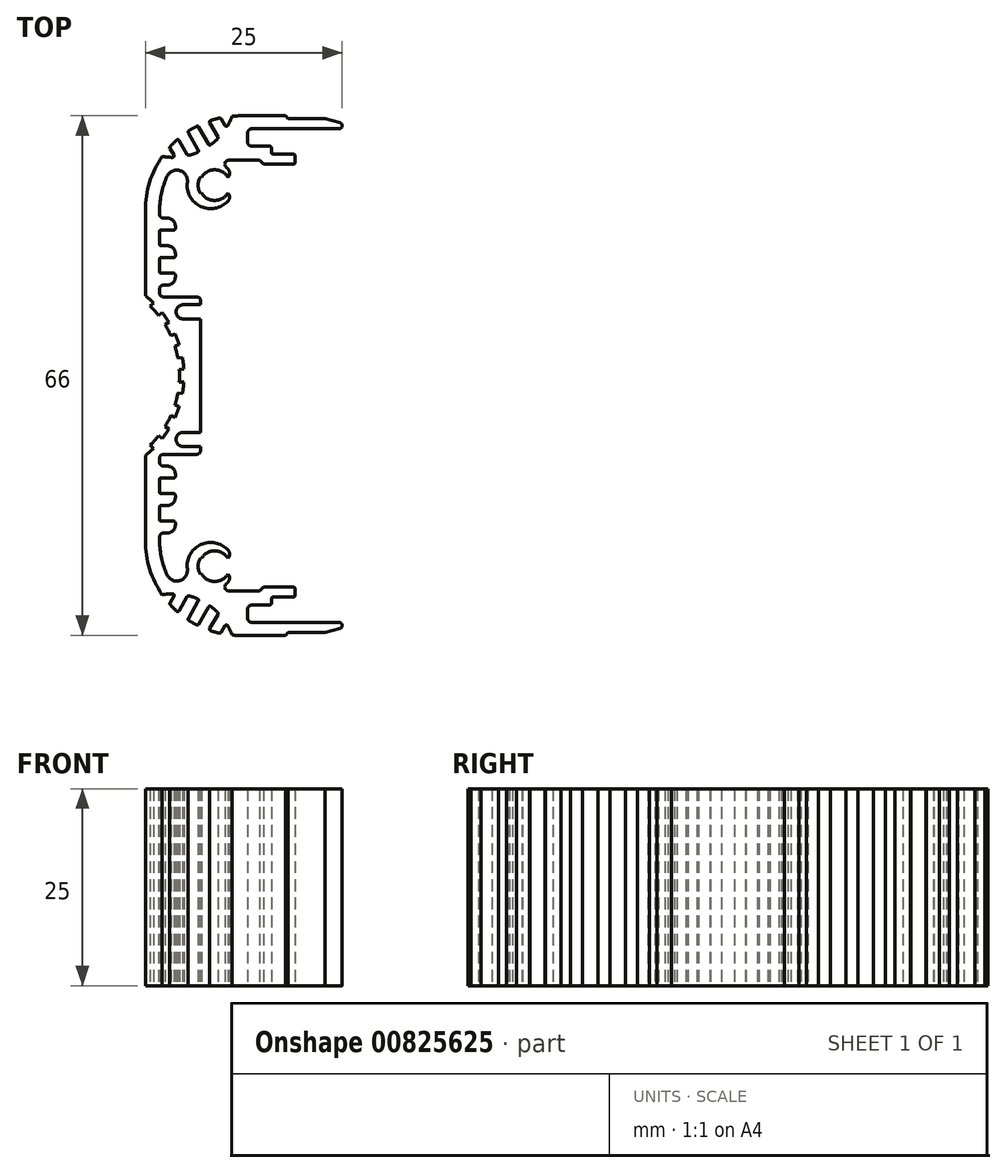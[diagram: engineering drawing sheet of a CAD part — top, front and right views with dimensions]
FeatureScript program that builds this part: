
annotation { "Feature Type Name" : "Feature", "Feature Type Description" : "" }
export const myFeature = defineFeature(function(context is Context, id is Id, definition is map)
    precondition{}
    {
        {
            var Q0;
            Q0=qCreatedBy(makeId("Top.planeOp"),FACE);
            var sketch = newSketch(context, id + "F0", { "sketchPlane" : qUnion([Q0])});
            skArc(sketch, "E0", {"start": v(4.8, 42) * mm, "mid": v(3.9, 41.1) * mm, "end": v(4.8, 40.2) * mm});
            skLineSegment(sketch, "E1", {"start": v(4.8, 42) * mm, "end": v(7, 42) * mm});
            skLineSegment(sketch, "E2", {"start": v(7, 42) * mm, "end": v(7, 42.5) * mm});
            skArc(sketch, "E3", {"start": v(7, 42.5) * mm, "mid": v(6.85, 42.85) * mm, "end": v(6.5, 43) * mm});
            skLineSegment(sketch, "E4", {"start": v(6.5, 43) * mm, "end": v(2.3, 43) * mm});
            skArc(sketch, "E5", {"start": v(1.8, 43.5) * mm, "mid": v(1.95, 43.15) * mm, "end": v(2.3, 43) * mm});
            skLineSegment(sketch, "E6", {"start": v(1.8, 43.5) * mm, "end": v(1.8, 44) * mm});
            skArc(sketch, "E7", {"start": v(2.3, 44.5) * mm, "mid": v(1.95, 44.35) * mm, "end": v(1.8, 44) * mm});
            skLineSegment(sketch, "E8", {"start": v(2.3, 44.5) * mm, "end": v(2.8, 44.5) * mm});
            skArc(sketch, "E9", {"start": v(2.8, 44.5) * mm, "mid": v(3.5, 44.8) * mm, "end": v(3.8, 45.5) * mm});
            skLineSegment(sketch, "E10", {"start": v(3.8, 45.5) * mm, "end": v(3.8, 45.8) * mm});
            skArc(sketch, "E11", {"start": v(3.8, 45.8) * mm, "mid": v(3.74, 45.94) * mm, "end": v(3.6, 46) * mm});
            skLineSegment(sketch, "E12", {"start": v(3.6, 46) * mm, "end": v(2, 46) * mm});
            skArc(sketch, "E13", {"start": v(1.8, 46.2) * mm, "mid": v(1.86, 46.06) * mm, "end": v(2, 46) * mm});
            skLineSegment(sketch, "E14", {"start": v(1.8, 46.2) * mm, "end": v(1.8, 47.8) * mm});
            skArc(sketch, "E15", {"start": v(2, 48) * mm, "mid": v(1.86, 47.94) * mm, "end": v(1.8, 47.8) * mm});
            skLineSegment(sketch, "E16", {"start": v(2, 48) * mm, "end": v(3.6, 48) * mm});
            skArc(sketch, "E17", {"start": v(3.6, 48) * mm, "mid": v(3.74, 48.06) * mm, "end": v(3.8, 48.2) * mm});
            skLineSegment(sketch, "E18", {"start": v(3.8, 48.2) * mm, "end": v(3.8, 48.5) * mm});
            skArc(sketch, "E19", {"start": v(3.8, 48.5) * mm, "mid": v(3.5, 49.2) * mm, "end": v(2.8, 49.5) * mm});
            skLineSegment(sketch, "E20", {"start": v(2.8, 49.5) * mm, "end": v(2, 49.5) * mm});
            skArc(sketch, "E21", {"start": v(1.8, 49.7) * mm, "mid": v(1.86, 49.56) * mm, "end": v(2, 49.5) * mm});
            skLineSegment(sketch, "E22", {"start": v(1.8, 49.7) * mm, "end": v(1.8, 51.3) * mm});
            skArc(sketch, "E23", {"start": v(2, 51.5) * mm, "mid": v(1.86, 51.44) * mm, "end": v(1.8, 51.3) * mm});
            skLineSegment(sketch, "E24", {"start": v(2, 51.5) * mm, "end": v(3.6, 51.5) * mm});
            skArc(sketch, "E25", {"start": v(3.6, 51.5) * mm, "mid": v(3.74, 51.56) * mm, "end": v(3.8, 51.7) * mm});
            skLineSegment(sketch, "E26", {"start": v(3.8, 51.7) * mm, "end": v(3.8, 52) * mm});
            skArc(sketch, "E27", {"start": v(3.8, 52) * mm, "mid": v(3.5, 52.7) * mm, "end": v(2.8, 53) * mm});
            skLineSegment(sketch, "E28", {"start": v(2.8, 53) * mm, "end": v(2.3, 53) * mm});
            skArc(sketch, "E29", {"start": v(1.8, 53.5) * mm, "mid": v(1.95, 53.15) * mm, "end": v(2.3, 53) * mm});
            skLineSegment(sketch, "E30", {"start": v(1.8, 53.5) * mm, "end": v(1.8, 54) * mm});
            skArc(sketch, "E31", {"start": v(2.76, 58.33) * mm, "mid": v(2.04, 56.22) * mm, "end": v(1.8, 54) * mm});
            skArc(sketch, "E32", {"start": v(5.32, 57.58) * mm, "mid": v(4.36, 59.05) * mm, "end": v(2.76, 58.33) * mm});
            skArc(sketch, "E33", {"start": v(5.32, 57.58) * mm, "mid": v(7.03, 54.48) * mm, "end": v(10.5, 55.16) * mm});
            skArc(sketch, "E34", {"start": v(10.5, 55.16) * mm, "mid": v(10.7, 55.69) * mm, "end": v(10.48, 56.2) * mm});
            skArc(sketch, "E35", {"start": v(7.11, 56.23) * mm, "mid": v(8.79, 55.25) * mm, "end": v(10.48, 56.2) * mm});
            skLineSegment(sketch, "E36", {"start": v(7.11, 56.23) * mm, "end": v(6.98, 56.15) * mm});
            skArc(sketch, "E37", {"start": v(6.98, 58.25) * mm, "mid": v(6.7, 57.2) * mm, "end": v(6.98, 56.15) * mm});
            skLineSegment(sketch, "E38", {"start": v(6.98, 58.25) * mm, "end": v(7.11, 58.17) * mm});
            skArc(sketch, "E39", {"start": v(10.48, 58.2) * mm, "mid": v(8.79, 59.15) * mm, "end": v(7.11, 58.17) * mm});
            skArc(sketch, "E40", {"start": v(10.48, 58.2) * mm, "mid": v(10.7, 58.71) * mm, "end": v(10.5, 59.24) * mm});
            skArc(sketch, "E41", {"start": v(10.5, 59.24) * mm, "mid": v(10.38, 59.36) * mm, "end": v(10.26, 59.47) * mm});
            skArc(sketch, "E42", {"start": v(10.59, 60.35) * mm, "mid": v(10.12, 60.02) * mm, "end": v(10.26, 59.47) * mm});
            skLineSegment(sketch, "E43", {"start": v(10.59, 60.35) * mm, "end": v(14.5, 60.35) * mm});
            skLineSegment(sketch, "E44", {"start": v(14.5, 60.35) * mm, "end": v(15, 59.85) * mm});
            skLineSegment(sketch, "E45", {"start": v(15, 59.85) * mm, "end": v(18.8, 59.85) * mm});
            skArc(sketch, "E46", {"start": v(18.8, 59.85) * mm, "mid": v(18.94, 59.9) * mm, "end": v(19, 60.05) * mm});
            skLineSegment(sketch, "E47", {"start": v(19, 60.05) * mm, "end": v(19, 60.95) * mm});
            skArc(sketch, "E48", {"start": v(19, 60.95) * mm, "mid": v(18.94, 61.1) * mm, "end": v(18.8, 61.15) * mm});
            skLineSegment(sketch, "E49", {"start": v(18.8, 61.15) * mm, "end": v(16.2, 61.15) * mm});
            skArc(sketch, "E50", {"start": v(16, 61.35) * mm, "mid": v(16.06, 61.2) * mm, "end": v(16.2, 61.15) * mm});
            skLineSegment(sketch, "E51", {"start": v(16, 61.35) * mm, "end": v(16, 61.95) * mm});
            skArc(sketch, "E52", {"start": v(16, 61.95) * mm, "mid": v(15.94, 62.1) * mm, "end": v(15.8, 62.15) * mm});
            skLineSegment(sketch, "E53", {"start": v(15.8, 62.15) * mm, "end": v(13.5, 62.15) * mm});
            skArc(sketch, "E54", {"start": v(13, 62.65) * mm, "mid": v(13.15, 62.3) * mm, "end": v(13.5, 62.15) * mm});
            skLineSegment(sketch, "E55", {"start": v(13, 62.65) * mm, "end": v(13, 63.85) * mm});
            skArc(sketch, "E56", {"start": v(13.5, 64.35) * mm, "mid": v(13.15, 64.2) * mm, "end": v(13, 63.85) * mm});
            skLineSegment(sketch, "E57", {"start": v(13.5, 64.35) * mm, "end": v(24.6, 64.35) * mm});
            skArc(sketch, "E58", {"start": v(24.6, 64.35) * mm, "mid": v(25, 64.7) * mm, "end": v(24.7, 65.14) * mm});
            skLineSegment(sketch, "E59", {"start": v(24.7, 65.14) * mm, "end": v(22.79, 65.65) * mm});
            skLineSegment(sketch, "E60", {"start": v(22.79, 65.65) * mm, "end": v(18.15, 65.65) * mm});
            skLineSegment(sketch, "E61", {"start": v(18.15, 65.65) * mm, "end": v(17.8, 66) * mm});
            skLineSegment(sketch, "E62", {"start": v(17.8, 66) * mm, "end": v(12, 66) * mm});
            skArc(sketch, "E63", {"start": v(12, 66) * mm, "mid": v(11.5, 65.99) * mm, "end": v(11, 65.96) * mm});
            skArc(sketch, "E64", {"start": v(10.46, 64.77) * mm, "mid": v(10.76, 65.36) * mm, "end": v(11, 65.96) * mm});
            skArc(sketch, "E65", {"start": v(10.11, 64.77) * mm, "mid": v(10.29, 64.67) * mm, "end": v(10.46, 64.77) * mm});
            skLineSegment(sketch, "E66", {"start": v(10.11, 64.77) * mm, "end": v(9.62, 65.62) * mm});
            skArc(sketch, "E67", {"start": v(9.62, 65.62) * mm, "mid": v(9.53, 65.7) * mm, "end": v(9.4, 65.72) * mm});
            skArc(sketch, "E68", {"start": v(9.4, 65.72) * mm, "mid": v(8.84, 65.58) * mm, "end": v(8.29, 65.41) * mm});
            skArc(sketch, "E69", {"start": v(8.29, 65.41) * mm, "mid": v(8.16, 65.3) * mm, "end": v(8.18, 65.12) * mm});
            skLineSegment(sketch, "E70", {"start": v(8.18, 65.12) * mm, "end": v(9.21, 63.33) * mm});
            skArc(sketch, "E71", {"start": v(9.18, 63.09) * mm, "mid": v(9.24, 63.2) * mm, "end": v(9.21, 63.33) * mm});
            skArc(sketch, "E72", {"start": v(8.32, 62.33) * mm, "mid": v(8.76, 62.7) * mm, "end": v(9.18, 63.09) * mm});
            skArc(sketch, "E73", {"start": v(8.02, 62.4) * mm, "mid": v(8.16, 62.3) * mm, "end": v(8.32, 62.33) * mm});
            skLineSegment(sketch, "E74", {"start": v(8.02, 62.4) * mm, "end": v(6.76, 64.58) * mm});
            skArc(sketch, "E75", {"start": v(6.76, 64.58) * mm, "mid": v(6.64, 64.68) * mm, "end": v(6.5, 64.66) * mm});
            skArc(sketch, "E76", {"start": v(6.5, 64.66) * mm, "mid": v(6, 64.4) * mm, "end": v(5.52, 64.1) * mm});
            skArc(sketch, "E77", {"start": v(5.52, 64.1) * mm, "mid": v(5.43, 63.98) * mm, "end": v(5.46, 63.83) * mm});
            skLineSegment(sketch, "E78", {"start": v(5.46, 63.83) * mm, "end": v(6.72, 61.64) * mm});
            skArc(sketch, "E79", {"start": v(6.63, 61.36) * mm, "mid": v(6.74, 61.48) * mm, "end": v(6.72, 61.64) * mm});
            skArc(sketch, "E80", {"start": v(5.54, 60.98) * mm, "mid": v(6.09, 61.15) * mm, "end": v(6.63, 61.36) * mm});
            skArc(sketch, "E81", {"start": v(5.31, 61.08) * mm, "mid": v(5.41, 61) * mm, "end": v(5.54, 60.98) * mm});
            skLineSegment(sketch, "E82", {"start": v(5.31, 61.08) * mm, "end": v(4.28, 62.87) * mm});
            skArc(sketch, "E83", {"start": v(4.28, 62.87) * mm, "mid": v(4.14, 62.97) * mm, "end": v(3.97, 62.92) * mm});
            skArc(sketch, "E84", {"start": v(3.97, 62.92) * mm, "mid": v(3.55, 62.52) * mm, "end": v(3.15, 62.1) * mm});
            skArc(sketch, "E85", {"start": v(3.15, 62.1) * mm, "mid": v(3.1, 62) * mm, "end": v(3.12, 61.87) * mm});
            skLineSegment(sketch, "E86", {"start": v(3.12, 61.87) * mm, "end": v(3.62, 61.02) * mm});
            skArc(sketch, "E87", {"start": v(3.44, 60.72) * mm, "mid": v(3.61, 60.82) * mm, "end": v(3.62, 61.02) * mm});
            skArc(sketch, "E88", {"start": v(2.14, 60.84) * mm, "mid": v(2.79, 60.75) * mm, "end": v(3.44, 60.72) * mm});
            skArc(sketch, "E89", {"start": v(2.14, 60.84) * mm, "mid": v(0.55, 57.58) * mm, "end": v(0, 54) * mm});
            skLineSegment(sketch, "E90", {"start": v(0, 54) * mm, "end": v(0, 43.13) * mm});
            skArc(sketch, "E91", {"start": v(1.01, 42.24) * mm, "mid": v(0.52, 42.7) * mm, "end": v(0, 43.13) * mm});
            skLineSegment(sketch, "E92", {"start": v(1.01, 42.24) * mm, "end": v(0.6, 41.83) * mm});
            skArc(sketch, "E93", {"start": v(1.68, 40.64) * mm, "mid": v(1.16, 41.25) * mm, "end": v(0.6, 41.83) * mm});
            skLineSegment(sketch, "E94", {"start": v(1.68, 40.64) * mm, "end": v(2.13, 41) * mm});
            skArc(sketch, "E95", {"start": v(2.98, 39.79) * mm, "mid": v(2.58, 40.4) * mm, "end": v(2.13, 41) * mm});
            skLineSegment(sketch, "E96", {"start": v(2.98, 39.79) * mm, "end": v(2.49, 39.48) * mm});
            skArc(sketch, "E97", {"start": v(3.24, 38.07) * mm, "mid": v(2.89, 38.79) * mm, "end": v(2.49, 39.48) * mm});
            skLineSegment(sketch, "E98", {"start": v(3.24, 38.07) * mm, "end": v(3.77, 38.3) * mm});
            skArc(sketch, "E99", {"start": v(4.3, 36.93) * mm, "mid": v(4.05, 37.63) * mm, "end": v(3.77, 38.3) * mm});
            skLineSegment(sketch, "E100", {"start": v(4.3, 36.93) * mm, "end": v(3.75, 36.75) * mm});
            skArc(sketch, "E101", {"start": v(4.13, 35.2) * mm, "mid": v(3.96, 35.98) * mm, "end": v(3.75, 36.75) * mm});
            skLineSegment(sketch, "E102", {"start": v(4.13, 35.2) * mm, "end": v(4.7, 35.3) * mm});
            skArc(sketch, "E103", {"start": v(4.88, 33.84) * mm, "mid": v(4.81, 34.57) * mm, "end": v(4.7, 35.3) * mm});
            skLineSegment(sketch, "E104", {"start": v(4.88, 33.84) * mm, "end": v(4.3, 33.8) * mm});
            skArc(sketch, "E105", {"start": v(4.3, 32.2) * mm, "mid": v(4.33, 33) * mm, "end": v(4.3, 33.8) * mm});
            skLineSegment(sketch, "E106", {"start": v(4.3, 32.2) * mm, "end": v(4.88, 32.16) * mm});
            skArc(sketch, "E107", {"start": v(4.7, 30.7) * mm, "mid": v(4.81, 31.43) * mm, "end": v(4.88, 32.16) * mm});
            skLineSegment(sketch, "E108", {"start": v(4.7, 30.7) * mm, "end": v(4.13, 30.8) * mm});
            skArc(sketch, "E109", {"start": v(3.75, 29.25) * mm, "mid": v(3.96, 30.02) * mm, "end": v(4.13, 30.8) * mm});
            skLineSegment(sketch, "E110", {"start": v(3.75, 29.25) * mm, "end": v(4.3, 29.07) * mm});
            skArc(sketch, "E111", {"start": v(3.77, 27.7) * mm, "mid": v(4.05, 28.37) * mm, "end": v(4.3, 29.07) * mm});
            skLineSegment(sketch, "E112", {"start": v(3.77, 27.7) * mm, "end": v(3.24, 27.93) * mm});
            skArc(sketch, "E113", {"start": v(2.49, 26.52) * mm, "mid": v(2.89, 27.21) * mm, "end": v(3.24, 27.93) * mm});
            skLineSegment(sketch, "E114", {"start": v(2.49, 26.52) * mm, "end": v(2.98, 26.21) * mm});
            skArc(sketch, "E115", {"start": v(2.13, 25) * mm, "mid": v(2.58, 25.6) * mm, "end": v(2.98, 26.21) * mm});
            skLineSegment(sketch, "E116", {"start": v(2.13, 25) * mm, "end": v(1.68, 25.36) * mm});
            skArc(sketch, "E117", {"start": v(0.6, 24.17) * mm, "mid": v(1.16, 24.75) * mm, "end": v(1.68, 25.36) * mm});
            skLineSegment(sketch, "E118", {"start": v(0.6, 24.17) * mm, "end": v(1.01, 23.76) * mm});
            skArc(sketch, "E119", {"start": v(0, 22.87) * mm, "mid": v(0.52, 23.3) * mm, "end": v(1.01, 23.76) * mm});
            skLineSegment(sketch, "E120", {"start": v(0, 22.87) * mm, "end": v(0, 12) * mm});
            skArc(sketch, "E121", {"start": v(0, 12) * mm, "mid": v(0.55, 8.42) * mm, "end": v(2.14, 5.16) * mm});
            skArc(sketch, "E122", {"start": v(3.44, 5.28) * mm, "mid": v(2.79, 5.25) * mm, "end": v(2.14, 5.16) * mm});
            skArc(sketch, "E123", {"start": v(3.62, 4.98) * mm, "mid": v(3.61, 5.18) * mm, "end": v(3.44, 5.28) * mm});
            skLineSegment(sketch, "E124", {"start": v(3.62, 4.98) * mm, "end": v(3.12, 4.13) * mm});
            skArc(sketch, "E125", {"start": v(3.12, 4.13) * mm, "mid": v(3.1, 4) * mm, "end": v(3.15, 3.9) * mm});
            skArc(sketch, "E126", {"start": v(3.15, 3.9) * mm, "mid": v(3.55, 3.48) * mm, "end": v(3.97, 3.08) * mm});
            skArc(sketch, "E127", {"start": v(3.97, 3.08) * mm, "mid": v(4.14, 3.03) * mm, "end": v(4.28, 3.13) * mm});
            skLineSegment(sketch, "E128", {"start": v(4.28, 3.13) * mm, "end": v(5.31, 4.92) * mm});
            skArc(sketch, "E129", {"start": v(5.54, 5.02) * mm, "mid": v(5.41, 5) * mm, "end": v(5.31, 4.92) * mm});
            skArc(sketch, "E130", {"start": v(6.63, 4.64) * mm, "mid": v(6.09, 4.85) * mm, "end": v(5.54, 5.02) * mm});
            skArc(sketch, "E131", {"start": v(6.72, 4.36) * mm, "mid": v(6.74, 4.52) * mm, "end": v(6.63, 4.64) * mm});
            skLineSegment(sketch, "E132", {"start": v(6.72, 4.36) * mm, "end": v(5.46, 2.17) * mm});
            skArc(sketch, "E133", {"start": v(5.46, 2.17) * mm, "mid": v(5.43, 2.02) * mm, "end": v(5.52, 1.9) * mm});
            skArc(sketch, "E134", {"start": v(5.52, 1.9) * mm, "mid": v(6, 1.6) * mm, "end": v(6.5, 1.34) * mm});
            skArc(sketch, "E135", {"start": v(6.5, 1.34) * mm, "mid": v(6.64, 1.32) * mm, "end": v(6.76, 1.42) * mm});
            skLineSegment(sketch, "E136", {"start": v(6.76, 1.42) * mm, "end": v(8.02, 3.6) * mm});
            skArc(sketch, "E137", {"start": v(8.32, 3.67) * mm, "mid": v(8.16, 3.7) * mm, "end": v(8.02, 3.6) * mm});
            skArc(sketch, "E138", {"start": v(9.18, 2.91) * mm, "mid": v(8.76, 3.3) * mm, "end": v(8.32, 3.67) * mm});
            skArc(sketch, "E139", {"start": v(9.21, 2.67) * mm, "mid": v(9.24, 2.8) * mm, "end": v(9.18, 2.91) * mm});
            skLineSegment(sketch, "E140", {"start": v(9.21, 2.67) * mm, "end": v(8.18, 0.88) * mm});
            skArc(sketch, "E141", {"start": v(8.18, 0.88) * mm, "mid": v(8.16, 0.7) * mm, "end": v(8.29, 0.59) * mm});
            skArc(sketch, "E142", {"start": v(8.29, 0.59) * mm, "mid": v(8.84, 0.42) * mm, "end": v(9.4, 0.28) * mm});
            skArc(sketch, "E143", {"start": v(9.4, 0.28) * mm, "mid": v(9.53, 0.3) * mm, "end": v(9.62, 0.38) * mm});
            skLineSegment(sketch, "E144", {"start": v(9.62, 0.38) * mm, "end": v(10.11, 1.23) * mm});
            skArc(sketch, "E145", {"start": v(10.46, 1.23) * mm, "mid": v(10.29, 1.33) * mm, "end": v(10.11, 1.23) * mm});
            skArc(sketch, "E146", {"start": v(11, 0.04) * mm, "mid": v(10.76, 0.64) * mm, "end": v(10.46, 1.23) * mm});
            skArc(sketch, "E147", {"start": v(11, 0.04) * mm, "mid": v(11.5, 0.01) * mm, "end": v(12, 0) * mm});
            skLineSegment(sketch, "E148", {"start": v(12, 0) * mm, "end": v(17.8, 0) * mm});
            skLineSegment(sketch, "E149", {"start": v(17.8, 0) * mm, "end": v(18.15, 0.35) * mm});
            skLineSegment(sketch, "E150", {"start": v(18.15, 0.35) * mm, "end": v(22.79, 0.35) * mm});
            skLineSegment(sketch, "E151", {"start": v(22.79, 0.35) * mm, "end": v(24.7, 0.86) * mm});
            skArc(sketch, "E152", {"start": v(24.7, 0.86) * mm, "mid": v(25, 1.3) * mm, "end": v(24.6, 1.65) * mm});
            skLineSegment(sketch, "E153", {"start": v(24.6, 1.65) * mm, "end": v(13.5, 1.65) * mm});
            skArc(sketch, "E154", {"start": v(13, 2.15) * mm, "mid": v(13.15, 1.8) * mm, "end": v(13.5, 1.65) * mm});
            skLineSegment(sketch, "E155", {"start": v(13, 2.15) * mm, "end": v(13, 3.35) * mm});
            skArc(sketch, "E156", {"start": v(13.5, 3.85) * mm, "mid": v(13.15, 3.7) * mm, "end": v(13, 3.35) * mm});
            skLineSegment(sketch, "E157", {"start": v(13.5, 3.85) * mm, "end": v(15.8, 3.85) * mm});
            skArc(sketch, "E158", {"start": v(15.8, 3.85) * mm, "mid": v(15.94, 3.9) * mm, "end": v(16, 4.05) * mm});
            skLineSegment(sketch, "E159", {"start": v(16, 4.05) * mm, "end": v(16, 4.65) * mm});
            skArc(sketch, "E160", {"start": v(16.2, 4.85) * mm, "mid": v(16.06, 4.8) * mm, "end": v(16, 4.65) * mm});
            skLineSegment(sketch, "E161", {"start": v(16.2, 4.85) * mm, "end": v(18.8, 4.85) * mm});
            skArc(sketch, "E162", {"start": v(18.8, 4.85) * mm, "mid": v(18.94, 4.9) * mm, "end": v(19, 5.05) * mm});
            skLineSegment(sketch, "E163", {"start": v(19, 5.05) * mm, "end": v(19, 5.95) * mm});
            skArc(sketch, "E164", {"start": v(19, 5.95) * mm, "mid": v(18.94, 6.1) * mm, "end": v(18.8, 6.15) * mm});
            skLineSegment(sketch, "E165", {"start": v(18.8, 6.15) * mm, "end": v(15, 6.15) * mm});
            skLineSegment(sketch, "E166", {"start": v(15, 6.15) * mm, "end": v(14.5, 5.65) * mm});
            skLineSegment(sketch, "E167", {"start": v(14.5, 5.65) * mm, "end": v(10.59, 5.65) * mm});
            skArc(sketch, "E168", {"start": v(10.26, 6.53) * mm, "mid": v(10.12, 5.98) * mm, "end": v(10.59, 5.65) * mm});
            skArc(sketch, "E169", {"start": v(10.26, 6.53) * mm, "mid": v(10.38, 6.64) * mm, "end": v(10.5, 6.76) * mm});
            skArc(sketch, "E170", {"start": v(10.5, 6.76) * mm, "mid": v(10.7, 7.29) * mm, "end": v(10.48, 7.8) * mm});
            skArc(sketch, "E171", {"start": v(7.11, 7.83) * mm, "mid": v(8.79, 6.85) * mm, "end": v(10.48, 7.8) * mm});
            skLineSegment(sketch, "E172", {"start": v(7.11, 7.83) * mm, "end": v(6.98, 7.75) * mm});
            skArc(sketch, "E173", {"start": v(6.98, 9.85) * mm, "mid": v(6.7, 8.8) * mm, "end": v(6.98, 7.75) * mm});
            skLineSegment(sketch, "E174", {"start": v(6.98, 9.85) * mm, "end": v(7.11, 9.78) * mm});
            skArc(sketch, "E175", {"start": v(10.48, 9.8) * mm, "mid": v(8.79, 10.75) * mm, "end": v(7.11, 9.77) * mm});
            skArc(sketch, "E176", {"start": v(10.48, 9.8) * mm, "mid": v(10.7, 10.31) * mm, "end": v(10.5, 10.84) * mm});
            skArc(sketch, "E177", {"start": v(10.5, 10.84) * mm, "mid": v(7.03, 11.52) * mm, "end": v(5.32, 8.42) * mm});
            skArc(sketch, "E178", {"start": v(2.76, 7.67) * mm, "mid": v(4.36, 6.95) * mm, "end": v(5.32, 8.42) * mm});
            skArc(sketch, "E179", {"start": v(1.8, 12) * mm, "mid": v(2.04, 9.78) * mm, "end": v(2.76, 7.67) * mm});
            skLineSegment(sketch, "E180", {"start": v(1.8, 12) * mm, "end": v(1.8, 12.5) * mm});
            skArc(sketch, "E181", {"start": v(2.3, 13) * mm, "mid": v(1.95, 12.85) * mm, "end": v(1.8, 12.5) * mm});
            skLineSegment(sketch, "E182", {"start": v(2.3, 13) * mm, "end": v(2.8, 13) * mm});
            skArc(sketch, "E183", {"start": v(2.8, 13) * mm, "mid": v(3.5, 13.3) * mm, "end": v(3.8, 14) * mm});
            skLineSegment(sketch, "E184", {"start": v(3.8, 14) * mm, "end": v(3.8, 14.3) * mm});
            skArc(sketch, "E185", {"start": v(3.8, 14.3) * mm, "mid": v(3.74, 14.44) * mm, "end": v(3.6, 14.5) * mm});
            skLineSegment(sketch, "E186", {"start": v(3.6, 14.5) * mm, "end": v(2, 14.5) * mm});
            skArc(sketch, "E187", {"start": v(1.8, 14.7) * mm, "mid": v(1.86, 14.56) * mm, "end": v(2, 14.5) * mm});
            skLineSegment(sketch, "E188", {"start": v(1.8, 14.7) * mm, "end": v(1.8, 16.3) * mm});
            skArc(sketch, "E189", {"start": v(2, 16.5) * mm, "mid": v(1.86, 16.44) * mm, "end": v(1.8, 16.3) * mm});
            skLineSegment(sketch, "E190", {"start": v(2, 16.5) * mm, "end": v(2.8, 16.5) * mm});
            skArc(sketch, "E191", {"start": v(2.8, 16.5) * mm, "mid": v(3.5, 16.8) * mm, "end": v(3.8, 17.5) * mm});
            skLineSegment(sketch, "E192", {"start": v(3.8, 17.5) * mm, "end": v(3.8, 17.8) * mm});
            skArc(sketch, "E193", {"start": v(3.8, 17.8) * mm, "mid": v(3.74, 17.94) * mm, "end": v(3.6, 18) * mm});
            skLineSegment(sketch, "E194", {"start": v(3.6, 18) * mm, "end": v(2, 18) * mm});
            skArc(sketch, "E195", {"start": v(1.8, 18.2) * mm, "mid": v(1.86, 18.06) * mm, "end": v(2, 18) * mm});
            skLineSegment(sketch, "E196", {"start": v(1.8, 18.2) * mm, "end": v(1.8, 19.8) * mm});
            skArc(sketch, "E197", {"start": v(2, 20) * mm, "mid": v(1.86, 19.94) * mm, "end": v(1.8, 19.8) * mm});
            skLineSegment(sketch, "E198", {"start": v(2, 20) * mm, "end": v(3.6, 20) * mm});
            skArc(sketch, "E199", {"start": v(3.6, 20) * mm, "mid": v(3.74, 20.06) * mm, "end": v(3.8, 20.2) * mm});
            skLineSegment(sketch, "E200", {"start": v(3.8, 20.2) * mm, "end": v(3.8, 20.5) * mm});
            skArc(sketch, "E201", {"start": v(3.8, 20.5) * mm, "mid": v(3.5, 21.2) * mm, "end": v(2.8, 21.5) * mm});
            skLineSegment(sketch, "E202", {"start": v(2.8, 21.5) * mm, "end": v(2.3, 21.5) * mm});
            skArc(sketch, "E203", {"start": v(1.8, 22) * mm, "mid": v(1.95, 21.65) * mm, "end": v(2.3, 21.5) * mm});
            skLineSegment(sketch, "E204", {"start": v(1.8, 22) * mm, "end": v(1.8, 22.5) * mm});
            skArc(sketch, "E205", {"start": v(2.3, 23) * mm, "mid": v(1.95, 22.85) * mm, "end": v(1.8, 22.5) * mm});
            skLineSegment(sketch, "E206", {"start": v(2.3, 23) * mm, "end": v(6.5, 23) * mm});
            skArc(sketch, "E207", {"start": v(6.5, 23) * mm, "mid": v(6.85, 23.15) * mm, "end": v(7, 23.5) * mm});
            skLineSegment(sketch, "E208", {"start": v(7, 23.5) * mm, "end": v(7, 24) * mm});
            skLineSegment(sketch, "E209", {"start": v(7, 24) * mm, "end": v(4.8, 24) * mm});
            skArc(sketch, "E210", {"start": v(4.8, 25.8) * mm, "mid": v(3.9, 24.9) * mm, "end": v(4.8, 24) * mm});
            skLineSegment(sketch, "E211", {"start": v(4.8, 25.8) * mm, "end": v(7, 25.8) * mm});
            skLineSegment(sketch, "E212", {"start": v(7, 25.8) * mm, "end": v(7, 40.2) * mm});
            skLineSegment(sketch, "E213", {"start": v(7, 40.2) * mm, "end": v(4.8, 40.2) * mm});
            skSolve(sketch);
        }
        {
            var Q0;
            Q0 = qSketchRegion(id + "F0", true);
            extrude(context, id + "F1", {"entities" : qUnion([Q0]), "depth" : 25 * mm, "offsetDistance" : 25 * mm});
        }
    });
